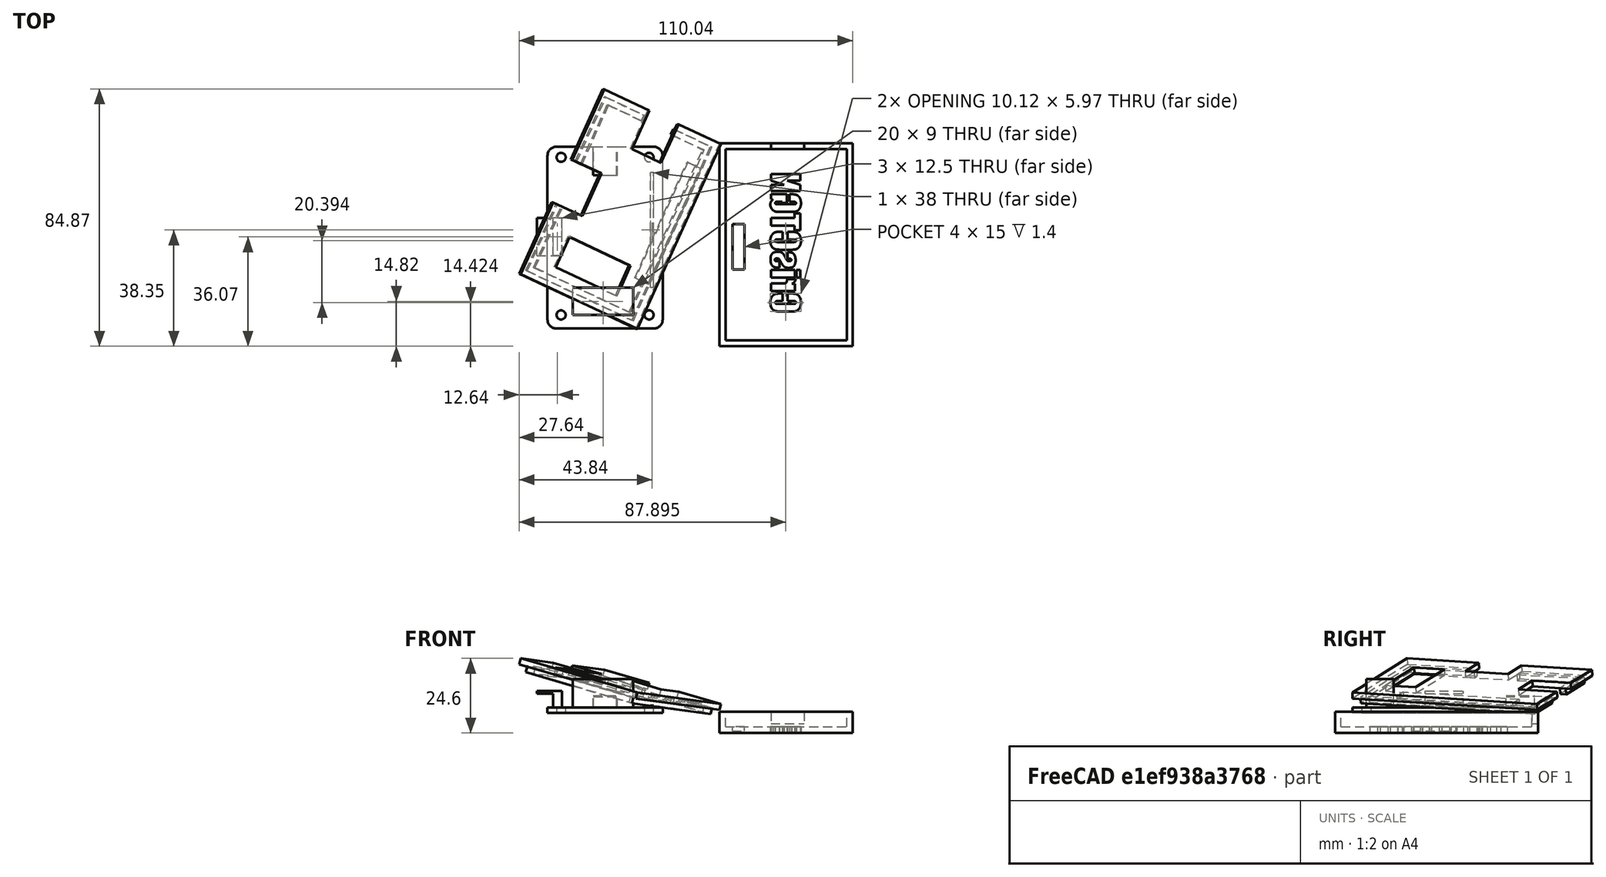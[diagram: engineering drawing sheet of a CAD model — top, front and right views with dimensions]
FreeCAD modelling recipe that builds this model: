
FCSTD DOCUMENT  (FreeCAD 0.21R33668 +26 (Git))
Label: busPiratev3_iteracion3
License: All rights reserved
LicenseURL: https://en.wikipedia.org/wiki/All_rights_reserved
objects: Part::Box×21, Part::Cut×17, Part::MultiFuse×6, Part::Cylinder×4, Part::Fillet×4, Part::Part2DObjectPython×1, Part::Extrusion×1, Part::Compound×1, Part::Mirroring×1
note: 56 computed .brp shape members not serialized (recipe doc carries the construction recipe); baked Part::Feature solids carry a one-line shape summary decoded from their .brp

FEATURE [Part::Box] Box  label="Placa"
  AttacherType = Attacher::AttachEngine3D
  Height = 1.8
  Length = 38
  Width = 60
FEATURE [Part::Box] Box001  label="Conector"
  AttacherType = Attacher::AttachEngine3D
  Height = 11.19
  Length = 20
  Placement = pos=(8.3,4.5,0) rot=(0,0,1;0rad)
  Width = 9
FEATURE [Part::Box] Box002  label="Cubo"
  AttacherType = Attacher::AttachEngine3D
  Height = 7.3
  Length = 8.3
  Placement = pos=(-3.5,21,-1) rot=(0,0,1;0rad)
  Width = 12.5
FEATURE [Part::Box] Box003  label="Cubo001"
  AttacherType = Attacher::AttachEngine3D
  Height = 6.3
  Length = 5.3
  Placement = pos=(-3.5,21,-1) rot=(0,0,1;0rad)
  Width = 12.5
FEATURE [Part::Box] Box004  label="Cubo002"
  AttacherType = Attacher::AttachEngine3D
  Height = 5.7
  Length = 8
  Placement = pos=(15,50.6,0) rot=(0,0,1;0rad)
  Width = 9.4
FEATURE [Part::Box] Box005  label="Cubo003"
  AttacherType = Attacher::AttachEngine3D
  Height = 3.5
  Length = 7.6
  Placement = pos=(15.2,50.6,1.8) rot=(0,0,1;0rad)
  Width = 9.4
FEATURE [Part::Box] Box006  label="Leds"
  AttacherType = Attacher::AttachEngine3D
  Height = 2.4
  Length = 1
  Placement = pos=(34,13.53,0) rot=(0,0,1;0rad)
  Width = 38
FEATURE [Part::Cut] Cut004  label="Conector001"
  Base = -> Box002
  Placement = pos=(0,3,1) rot=(0,0,1;0rad)
  Tool = -> Box003
FEATURE [Part::Cut] Cut005
  Base = -> Box004
  Tool = -> Box005
FEATURE [Part::Cylinder] Cylinder  label="hueco de tornillo 1"
  Angle = 360
  AttacherType = Attacher::AttachEngine3D
  FirstAngle = 0
  Height = 10
  Placement = pos=(4.5,4.5,0) rot=(0,0,1;0rad)
  Radius = 1.5
  SecondAngle = 0
FEATURE [Part::Cylinder] Cylinder001  label="hueco de tornillo 002"
  Angle = 360
  AttacherType = Attacher::AttachEngine3D
  FirstAngle = 0
  Height = 10
  Placement = pos=(33.5,4.5,0) rot=(0,0,1;0rad)
  Radius = 1.5
  SecondAngle = 0
FEATURE [Part::Cylinder] Cylinder002  label="hueco de tornillo 003"
  Angle = 360
  AttacherType = Attacher::AttachEngine3D
  FirstAngle = 0
  Height = 10
  Placement = pos=(4.5,56.5,0) rot=(0,0,1;0rad)
  Radius = 1.5
  SecondAngle = 0
FEATURE [Part::Cylinder] Cylinder003  label="hueco de tornillo 004"
  Angle = 360
  AttacherType = Attacher::AttachEngine3D
  FirstAngle = 0
  Height = 10
  Placement = pos=(33.5,56.5,0) rot=(0,0,1;0rad)
  Radius = 1.5
  SecondAngle = 0
FEATURE [Part::MultiFuse] Fusion
  Shapes = -> [Box001,Box]
FEATURE [Part::Cut] Cut
  Base = -> Fusion
  Tool = -> Cylinder002
FEATURE [Part::Cut] Cut001
  Base = -> Cut
  Tool = -> Cylinder
FEATURE [Part::Cut] Cut002
  Base = -> Cut001
  Tool = -> Cylinder003
FEATURE [Part::Cut] Cut003
  Base = -> Cut002
  Tool = -> Cylinder001
FEATURE [Part::Fillet] Fillet
  Base = -> Cut003
  Edges = 1 edges r=3: [Edge13]
FEATURE [Part::Fillet] Fillet001
  Base = -> Fillet
  Edges = 1 edges r=3: [Edge22]
FEATURE [Part::Fillet] Fillet002
  Base = -> Fillet001
  Edges = 1 edges r=3: [Edge23]
FEATURE [Part::Fillet] Fillet003
  Base = -> Fillet002
  Edges = 1 edges r=3: [Edge23]
FEATURE [Part::MultiFuse] Fusion001
  Shapes = -> [Fillet003,Cut004]
FEATURE [Part::MultiFuse] Fusion002
  Shapes = -> [Fusion001,Cut005]
FEATURE [Part::MultiFuse] Fusion003
  Placement = pos=(-42,6.5,-2) rot=(0,0,1;0rad)
  Shapes = -> [Fusion002,Box006]
FEATURE [Part::Box] Box007  label="Cubo004"
  AttacherType = Attacher::AttachEngine3D
  Height = 2
  Length = 44
  Width = 67
FEATURE [Part::Box] Box008  label="Conector Principal Bus"
  AttacherType = Attacher::AttachEngine3D
  Height = 10
  Length = 23
  Placement = pos=(10,7,-3) rot=(0,0,1;0rad)
  Width = 11
FEATURE [Part::Cut] Cut006
  Base = -> Box007
  Tool = -> Box008
FEATURE [Part::Box] Box009  label="Conector Lateral"
  AttacherType = Attacher::AttachEngine3D
  Height = 10
  Length = 11
  Placement = pos=(0,26,-1) rot=(0,0,1;0rad)
  Width = 15.5
FEATURE [Part::Cut] Cut007
  Base = -> Cut006
  Tool = -> Box009
FEATURE [Part::Box] Box010  label="Conector USB"
  AttacherType = Attacher::AttachEngine3D
  Height = 10
  Length = 11
  Placement = pos=(17,53,-1) rot=(0,0,1;0rad)
  Width = 15
FEATURE [Part::Cut] Cut008
  Base = -> Cut007
  Tool = -> Box010
FEATURE [Part::Box] Box011  label="Cubo005"
  AttacherType = Attacher::AttachEngine3D
  Height = 7
  Length = 44
  Width = 67
FEATURE [Part::Box] Box012  label="Cubo006"
  AttacherType = Attacher::AttachEngine3D
  Height = 10
  Length = 40
  Placement = pos=(2,2,2) rot=(0,0,1;0rad)
  Width = 63
FEATURE [Part::Cut] Cut009
  Base = -> Box011
  Tool = -> Box012
FEATURE [Part::Box] Box013  label="Cubo007"
  AttacherType = Attacher::AttachEngine3D
  Height = 10
  Length = 5
  Placement = pos=(36.5,15,-3) rot=(0,0,1;0rad)
  Width = 42
FEATURE [Part::Box] Box014  label="Cubo008"
  AttacherType = Attacher::AttachEngine3D
  Height = 10
  Length = 11
  Placement = pos=(17,63,3) rot=(0,0,1;0rad)
  Width = 11
FEATURE [Part::Part2DObjectPython] ShapeString  label="CrisCTGN"  # Draft 2D object (typed FeaturePython)
  FontFile = <path>
  MakeFace = true
  Placement = pos=(0,0,0) rot=(1,0,0;3.14159rad)
  Size = 10
  String = CrisCTGN
  Tracking = 0
FEATURE [Part::Extrusion] Extrude
  Base = -> ShapeString
  Dir = (0,-1e-16,-1)
  DirMode = 2
  FaceMakerClass = Part::FaceMakerBullseye
  LengthFwd = 2
  LengthRev = 0
  Placement = pos=(17,11,2) rot=(0,0,1;1.5708rad)
  Solid = false
  Symmetric = false
FEATURE [Part::Cut] Cut017
  Base = -> Cut008
  Placement = pos=(2.87189,0.96148,0) rot=(0,0,1;0rad)
  Tool = -> Box013
FEATURE [Part::Cut] Cut018
  Base = -> Cut009
  Tool = -> Box014
FEATURE [Part::Cut] Cut019
  Base = -> Cut018
  Placement = pos=(14.7,0.68386,-8.6) rot=(0,0,1;0rad)
  Tool = -> Extrude
FEATURE [Part::Box] Box015  label="Cubo009"
  AttacherType = Attacher::AttachEngine3D
  Height = 1
  Length = 8
  Placement = pos=(38,15,0) rot=(0,0,1;0rad)
  Width = 44
FEATURE [Part::MultiFuse] Fusion004
  Placement = pos=(1,0,0) rot=(0,0,1;0rad)
  Shapes = -> [Cut017,Box015]
FEATURE [Part::Compound] Compound
  Links = -> [Cut019]
FEATURE [Part::Box] Box016  label="Cubo010"
  AttacherType = Attacher::AttachEngine3D
  Height = 2.5
  Length = 4
  Placement = pos=(19,26,-8) rot=(0,0,1;0rad)
  Width = 15
FEATURE [Part::Cut] Cut020
  Base = -> Compound
  Tool = -> Box016
FEATURE [Part::Box] Box017  label="Cubo011"
  AttacherType = Attacher::AttachEngine3D
  Height = 2
  Length = 40
  Placement = pos=(6,3,2) rot=(0,0,1;0rad)
  Width = 63
FEATURE [Part::Box] Box018  label="Cubo012"
  AttacherType = Attacher::AttachEngine3D
  Height = 2
  Length = 36
  Placement = pos=(8,5,2) rot=(0,0,1;0rad)
  Width = 59
FEATURE [Part::Cut] Cut021
  Base = -> Box017
  Tool = -> Box018
FEATURE [Part::Box] Box019  label="Cubo013"
  AttacherType = Attacher::AttachEngine3D
  Height = 10
  Length = 10
  Placement = pos=(1,27,0) rot=(0,0,1;0rad)
  Width = 15.5
FEATURE [Part::Cut] Cut022
  Base = -> Cut021
  Tool = -> Box019
FEATURE [Part::Box] Box020  label="Cubo014"
  AttacherType = Attacher::AttachEngine3D
  Height = 10
  Length = 11
  Placement = pos=(20.9,58,1) rot=(0,0,1;0rad)
  Width = 10
FEATURE [Part::Cut] Cut023
  Base = -> Cut022
  Tool = -> Box020
FEATURE [Part::MultiFuse] Fusion005
  Placement = pos=(62.5,-0.5,1) rot=(0,1,0;3.14159rad)
  Shapes = -> [Fusion004,Cut023]
FEATURE [Part::Mirroring] Mirror  label="Fusion005 (reflejado)"
  Base = (-3.85173,-14.5068,-4.87098)
  Normal = (0.968112,-0.212494,-0.132685)
  Source = -> Fusion005
note: 1 file-system path scrubbed to <path> (originals preserved in the JSON sidecar)
